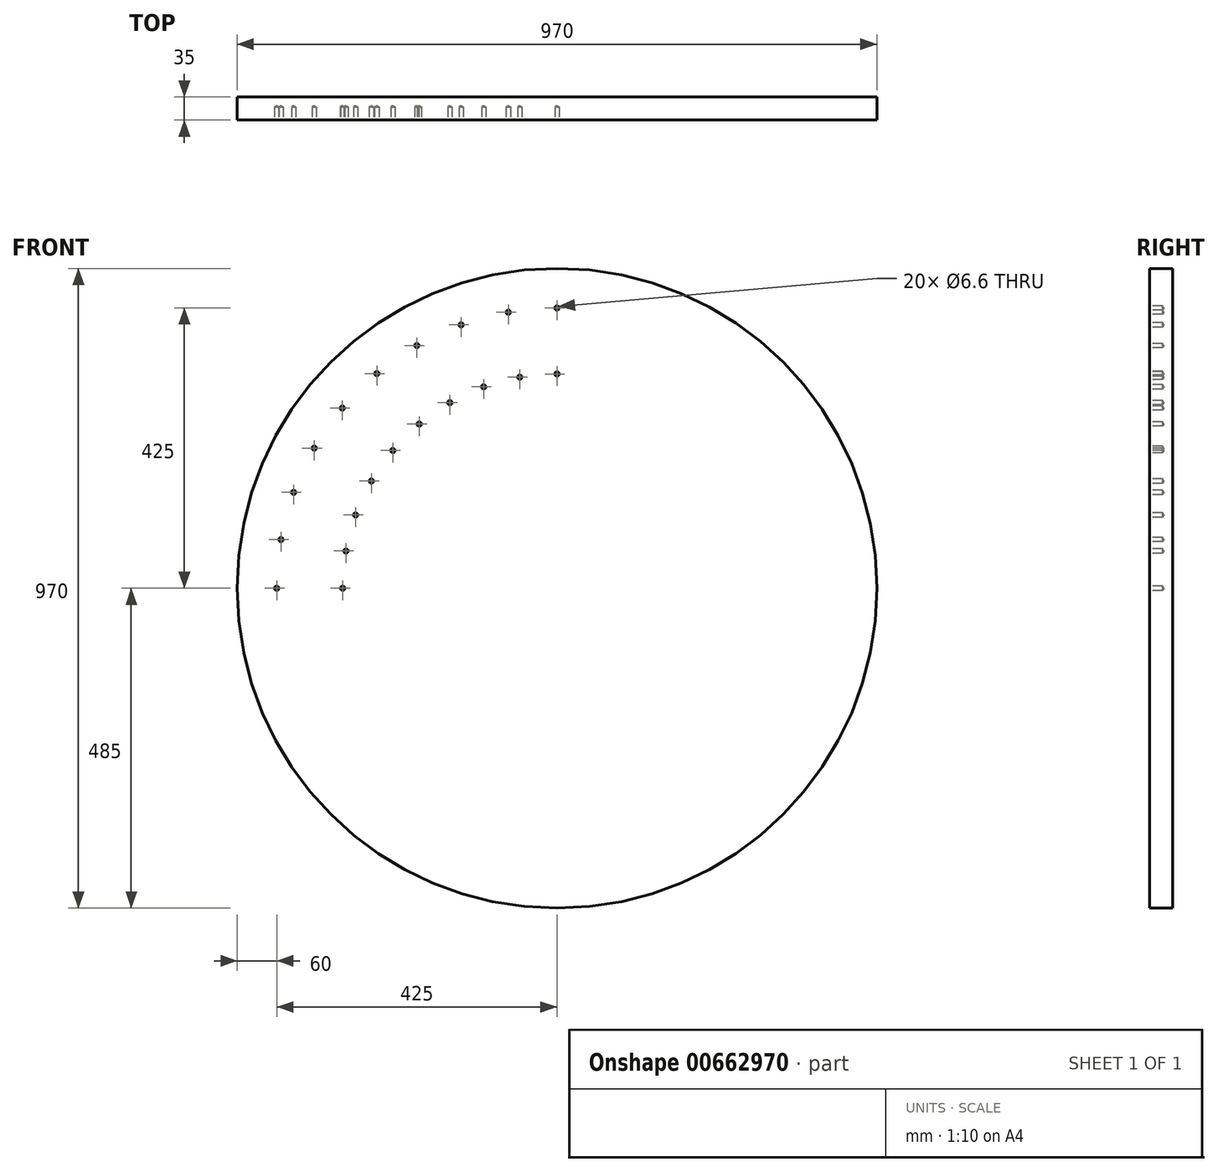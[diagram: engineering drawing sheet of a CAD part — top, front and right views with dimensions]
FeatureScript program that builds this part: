
annotation { "Feature Type Name" : "Feature", "Feature Type Description" : "" }
export const myFeature = defineFeature(function(context is Context, id is Id, definition is map)
    precondition{}
    {
        {
            var Q0;
            Q0=qCreatedBy(makeId("Front.planeOp"),FACE);
            var sketch = newSketch(context, id + "F0", { "sketchPlane" : qUnion([Q0])});
            skCircle(sketch, "E0", {"center": v(0, 0) * mm, "radius": 485 * mm});
            skCircle(sketch, "E1", {"center": v(0, 0) * mm, "radius": 325 * mm, "construction": true});
            skCircle(sketch, "E2", {"center": v(0, 0) * mm, "radius": 425 * mm, "construction": true});
            skPoint(sketch, "E3", {"position": v(-325, 0) * mm});
            skPoint(sketch, "E4", {"position": v(-425, 0) * mm});
            skLineSegment(sketch, "E5", {"start": v(-425, 0) * mm, "end": v(-325, 0) * mm, "construction": true});
            skLineSegment(sketch, "E6", {"start": v(-325, 0) * mm, "end": v(0, 0) * mm, "construction": true});
            skPoint(sketch, "E7.1.0", {"position": v(-418.54, 73.8) * mm});
            skPoint(sketch, "E7.1.1", {"position": v(-320.06, 56.44) * mm});
            skPoint(sketch, "E7.2.0", {"position": v(-399.37, 145.36) * mm});
            skPoint(sketch, "E7.2.1", {"position": v(-305.4, 111.16) * mm});
            skPoint(sketch, "E7.3.0", {"position": v(-368.06, 212.5) * mm});
            skPoint(sketch, "E7.3.1", {"position": v(-281.46, 162.5) * mm});
            skPoint(sketch, "E7.4.0", {"position": v(-325.57, 273.18) * mm});
            skPoint(sketch, "E7.4.1", {"position": v(-248.96, 208.9) * mm});
            skPoint(sketch, "E7.5.0", {"position": v(-273.18, 325.57) * mm});
            skPoint(sketch, "E7.5.1", {"position": v(-208.9, 248.96) * mm});
            skPoint(sketch, "E7.6.0", {"position": v(-212.5, 368.06) * mm});
            skPoint(sketch, "E7.6.1", {"position": v(-162.5, 281.46) * mm});
            skPoint(sketch, "E7.7.0", {"position": v(-145.36, 399.37) * mm});
            skPoint(sketch, "E7.7.1", {"position": v(-111.16, 305.4) * mm});
            skPoint(sketch, "E7.8.0", {"position": v(-73.8, 418.54) * mm});
            skPoint(sketch, "E7.8.1", {"position": v(-56.44, 320.06) * mm});
            skPoint(sketch, "E7.9.0", {"position": v(0, 425) * mm});
            skPoint(sketch, "E7.9.1", {"position": v(0, 325) * mm});
            skLineSegment(sketch, "E7.anchor1", {"start": v(0, 0) * mm, "end": v(-425, 0) * mm, "construction": true});
            skLineSegment(sketch, "E7.anchor2", {"start": v(0, 0) * mm, "end": v(0, 425) * mm, "construction": true});
            skSolve(sketch);
        }
        {
            var Q0;
            Q0=makeQuery(id+"F0.imprint","IMPRINT",FACE,{"disambiguationData":[TD([[makeQuery(id+"F0.imprint","IMPRINT",EDGE,{"derivedFrom":sQuery(id+"F0.wireOp",EDGE,"E0")}),1.0]])]});
            extrude(context, id + "F1", {"entities" : qUnion([Q0]), "oppositeDirection" : true, "depth" : 35 * mm, "offsetDistance" : 25 * mm});
        }
        {
            var Q0;
            Q0=sQuery(id+"F0.wireOp",VERTEX,"E3");
            var Q1;
            Q1=sQuery(id+"F0.wireOp",VERTEX,"E7.1.1");
            var Q2;
            Q2=sQuery(id+"F0.wireOp",VERTEX,"E7.2.1");
            var Q3;
            Q3=sQuery(id+"F0.wireOp",VERTEX,"E7.3.1");
            var Q4;
            Q4=sQuery(id+"F0.wireOp",VERTEX,"E7.4.1");
            var Q5;
            Q5=sQuery(id+"F0.wireOp",VERTEX,"E7.5.1");
            var Q6;
            Q6=sQuery(id+"F0.wireOp",VERTEX,"E7.6.1");
            var Q7;
            Q7=sQuery(id+"F0.wireOp",VERTEX,"E7.7.1");
            var Q8;
            Q8=sQuery(id+"F0.wireOp",VERTEX,"E7.8.1");
            var Q9;
            Q9=sQuery(id+"F0.wireOp",VERTEX,"E7.9.1");
            var Q10;
            Q10=sQuery(id+"F0.wireOp",VERTEX,"E7.9.0");
            var Q11;
            Q11=sQuery(id+"F0.wireOp",VERTEX,"E7.8.0");
            var Q12;
            Q12=sQuery(id+"F0.wireOp",VERTEX,"E7.7.0");
            var Q13;
            Q13=sQuery(id+"F0.wireOp",VERTEX,"E7.6.0");
            var Q14;
            Q14=sQuery(id+"F0.wireOp",VERTEX,"E7.5.0");
            var Q15;
            Q15=sQuery(id+"F0.wireOp",VERTEX,"E7.4.0");
            var Q16;
            Q16=sQuery(id+"F0.wireOp",VERTEX,"E7.3.0");
            var Q17;
            Q17=sQuery(id+"F0.wireOp",VERTEX,"E7.2.0");
            var Q18;
            Q18=sQuery(id+"F0.wireOp",VERTEX,"E7.1.0");
            var Q19;
            Q19=sQuery(id+"F0.wireOp",VERTEX,"E4");
            var Q20;
            Q20=makeQuery(id+"F1.opExtrude","SWEPT_BODY",BODY,{"disambiguationData":[OSD([sQuery(id+"F0.wireOp",EDGE,"E0")])]});
            hole(context, id + "F2", {"style" : HoleStyle.SIMPLE, "endStyle" : HoleEndStyle.BLIND, "standardTappedOrClearance" : lookupTablePath({ "fit" : "Normal", "standard" : "ISO", "size" : "M6", "type" : "Clearance" }), "standardBlindInLast" : lookupTablePath({ "fit" : "Normal", "standard" : "ISO", "engagement" : "75%", "pitch" : "1 mm", "size" : "M6", "type" : "Clearance & tapped" }), "holeDiameter" : 6.6 * mm, "majorDiameter" : 5 * mm, "holeDepth" : 19.75 * mm, "isTappedThrough" : true, "tappedDepth" : 16 * mm, "tapClearance" : 3, "locations" : qUnion([Q0, Q1, Q2, Q3, Q4, Q5, Q6, Q7, Q8, Q9, Q10, Q11, Q12, Q13, Q14, Q15, Q16, Q17, Q18, Q19]), "scope" : qUnion([Q20])});
        }
    });
